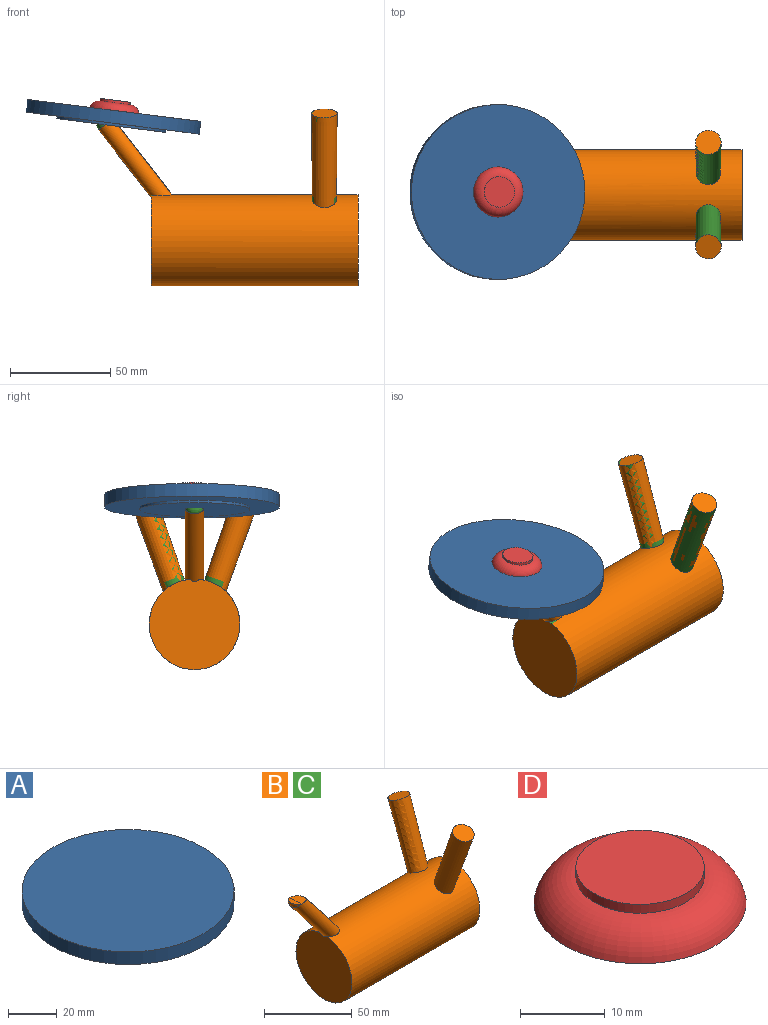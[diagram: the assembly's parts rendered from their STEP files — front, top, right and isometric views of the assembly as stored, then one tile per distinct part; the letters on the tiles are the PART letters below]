
ASSEMBLY  parts=4 mates=2
PART A: 5 faces, bbox 87.1x87.1x7.6 mm
  f0: cylinder r=43.57mm len=87.14mm, axis (0,0,-1), area 1738.3mm2, adj f1,f2
  f1: plane 87.14x87.14mm, normal (0,0,1), area 5963.5mm2, adj f0
  f2: plane 87.14x87.14mm, normal (0,0,-1), area 3619.4mm2, adj f0,f3
  f3: cylinder r=27.32mm len=54.63mm, axis (0,0,1), area 218mm2, adj f2,f4
  f4: plane 54.63x54.63mm, normal (0,0,-1), area 2344.2mm2, adj f3
PART B: 15 faces, bbox 130.1x64x88 mm
  f0: cylinder r=22.59mm len=103.08mm, axis (-1,0,0), area 14316.6mm2, adj f1,f2,f3,f5,f7,f8,f9,f10
  f1: cylinder r=4.57mm len=43.54mm, axis (0.61,0,-0.79), area 1137.5mm2, adj f0,f2,f8,f10,f11,f12
  f2: plane 45.17x45.04mm, normal (-1,0,0), area 1598.4mm2, adj f0,f1
  f3: plane 45.17x45.17mm, normal (1,0,0), area 1602.5mm2, adj f0
  f4: plane 12.72x11.98mm, normal (0,0.33,0.94), area 127.1mm2, adj f5
  f5: cone r=6.36mm half-angle=0.5deg, axis (0,0.33,0.94), area 1801.1mm2, adj f0,f4
  f6: plane 12.72x11.98mm, normal (0,-0.33,0.94), area 127.1mm2, adj f7
  f7: cone r=6.36mm half-angle=0.5deg, axis (0,-0.33,0.94), area 1801.1mm2, adj f0,f6
  f8: plane 34.18x26.73mm, normal (0,-1,0), area 7.8mm2, adj f0,f1,f9,f11
  f9: plane 34.16x26.49mm, normal (0.79,0,0.61), area 109.7mm2, adj f0,f8,f10,f11
  f10: plane 34.18x26.73mm, normal (0,1,0), area 7.8mm2, adj f0,f1,f9,f11
  f11: plane 9.15x7.13mm, normal (0.13,0,0.99), area 53.2mm2, adj f1,f8,f9,f10,f13
  f12: revolved ~9.09x4.07mm, area 28.6mm2, adj f1,f13,f14
  f13: revolved ~9.09x0.04mm, area 0.4mm2, adj f11,f12,f14
  f14: plane 9.09x4.01mm, normal (0.16,0,0.99), area 28.2mm2, adj f12,f13
PART C: same geometry as B
PART D: 4 faces, bbox 27.4x27.4x6.4 mm
  f0: plane 24.99x24.99mm, normal (0,0,-1), area 490.6mm2, adj f1
  f1: torus R=7.58mm, axis (0,0,-1), area 440.4mm2, adj f0,f2
  f2: cylinder r=7.58mm len=15.16mm, axis (0,0,-1), area 60.5mm2, adj f1,f3
  f3: plane 15.16x15.16mm, normal (0,0,1), area 180.4mm2, adj f2
PLACE A rot(axis=(0,1,0),7.2deg) t=(-29.54,0.73,11.79)mm
PLACE B t=(28.01,-0.56,-22.46)mm
PLACE C t=(28.01,-0.56,-22.46)mm
PLACE D rot(axis=(0,1,0),7.2deg) t=(-28.86,3.28,11.71)mm
MATE fastened A.f3 <-> C.f11  axis (-0.13,0,-0.99) through (-30.23,-0.56,10.6)mm
MATE fastened D.f1 <-> A.f0  axis (-0.13,0,-0.99) through (-28.75,0.73,18.09)mm
